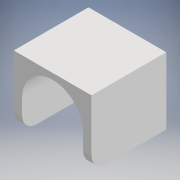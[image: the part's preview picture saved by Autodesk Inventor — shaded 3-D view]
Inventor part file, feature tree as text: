
AUTODESK INVENTOR PART (.ipt)
format: ipt  version: 2020 (Build 240168000, 168)  size: 140,800 bytes
history: native  units: mm
features: extrude x3, sketch x2, fillet x1, other x1, projected_geometry x1
ambient origin geometry x8: Origin, YZ Plane, XZ Plane, XY Plane, X Axis, Y Axis, Z Axis, Center Point
bodies: Solid1 (feature_tree)
feature tree (8):
  extrude  "BocnaStrana"  Depth=26.0mm
  extrude  "Tijelo"  Depth=2.0mm
  fillet  "Rubnik"  Radius=10.2mm
  extrude  "Extrusion3"  Depth=10.2mm
  other  "StranaDoKotaca"
  sketch  "Sketch2"  dims[d0=20.4mm d1=26.0mm]
  sketch  "Sketch3"  dims[d4=2.0mm d5=7.0mm d6=10.2mm d7=10.2mm d10=2.0mm d11=0.0mm d12=20.4mm d13=23.0mm d14=0.0mm d15=5.0mm d16=2.0mm d17=0.0mm]
  projected_geometry  "Projected Loop1"
